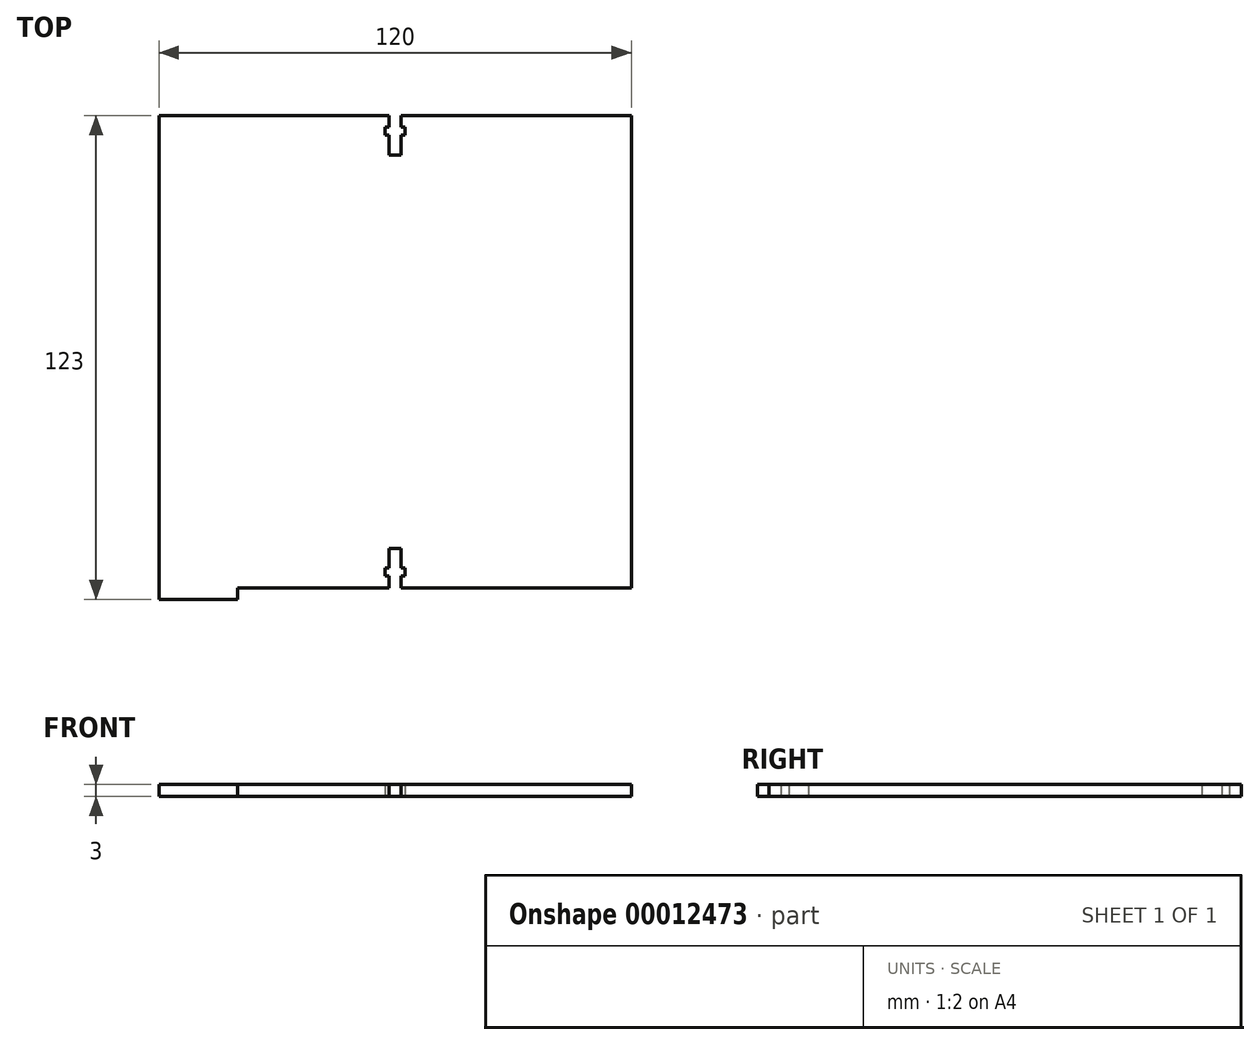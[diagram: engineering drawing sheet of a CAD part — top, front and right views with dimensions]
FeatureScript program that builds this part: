
annotation { "Feature Type Name" : "Feature", "Feature Type Description" : "" }
export const myFeature = defineFeature(function(context is Context, id is Id, definition is map)
    precondition{}
    {
        {
            var Q0;
            Q0=qCreatedBy(makeId("Top.planeOp"),FACE);
            var sketch = newSketch(context, id + "F0", { "sketchPlane" : qUnion([Q0])});
            skLineSegment(sketch, "E0.bottom", {"start": v(-57.37, 59.42) * mm, "end": v(62.63, 59.42) * mm});
            skLineSegment(sketch, "E0.top", {"start": v(-57.37, -60.58) * mm, "end": v(62.63, -60.58) * mm});
            skLineSegment(sketch, "E0.left", {"start": v(-57.37, 59.42) * mm, "end": v(-57.37, -60.58) * mm});
            skLineSegment(sketch, "E0.right", {"start": v(62.63, 59.42) * mm, "end": v(62.63, -60.58) * mm});
            skLineSegment(sketch, "E1.bottom", {"start": v(-57.37, 59.42) * mm, "end": v(-37.37, 59.42) * mm});
            skLineSegment(sketch, "E1.top", {"start": v(-57.37, 62.42) * mm, "end": v(-37.37, 62.42) * mm});
            skLineSegment(sketch, "E1.left", {"start": v(-57.37, 59.42) * mm, "end": v(-57.37, 62.42) * mm});
            skLineSegment(sketch, "E1.right", {"start": v(-37.37, 59.42) * mm, "end": v(-37.37, 62.42) * mm});
            skLineSegment(sketch, "E2.bottom", {"start": v(62.63, 59.42) * mm, "end": v(42.63, 59.42) * mm});
            skLineSegment(sketch, "E2.top", {"start": v(62.63, 62.42) * mm, "end": v(42.63, 62.42) * mm});
            skLineSegment(sketch, "E2.left", {"start": v(62.63, 59.42) * mm, "end": v(62.63, 62.42) * mm});
            skLineSegment(sketch, "E2.right", {"start": v(42.63, 59.42) * mm, "end": v(42.63, 62.42) * mm});
            skLineSegment(sketch, "E3.bottom", {"start": v(-57.37, -60.58) * mm, "end": v(-37.37, -60.58) * mm});
            skLineSegment(sketch, "E3.top", {"start": v(-57.37, -63.58) * mm, "end": v(-37.37, -63.58) * mm});
            skLineSegment(sketch, "E3.left", {"start": v(-57.37, -60.58) * mm, "end": v(-57.37, -63.58) * mm});
            skLineSegment(sketch, "E3.right", {"start": v(-37.37, -60.58) * mm, "end": v(-37.37, -63.58) * mm});
            skLineSegment(sketch, "E4.bottom", {"start": v(62.63, -60.58) * mm, "end": v(42.63, -60.58) * mm});
            skLineSegment(sketch, "E4.top", {"start": v(62.63, -63.58) * mm, "end": v(42.63, -63.58) * mm});
            skLineSegment(sketch, "E4.left", {"start": v(62.63, -60.58) * mm, "end": v(62.63, -63.58) * mm});
            skLineSegment(sketch, "E4.right", {"start": v(42.63, -60.58) * mm, "end": v(42.63, -63.58) * mm});
            skLineSegment(sketch, "E5", {"start": v(-57.37, -0.58) * mm, "end": v(62.63, -0.58) * mm, "construction": true});
            skLineSegment(sketch, "E6", {"start": v(2.63, 59.42) * mm, "end": v(2.63, -60.58) * mm, "construction": true});
            skLineSegment(sketch, "E7", {"start": v(4.13, 59.42) * mm, "end": v(4.13, 56.42) * mm});
            skLineSegment(sketch, "E8", {"start": v(4.13, 56.42) * mm, "end": v(5.13, 56.42) * mm});
            skLineSegment(sketch, "E9", {"start": v(5.13, 56.42) * mm, "end": v(5.13, 54.42) * mm});
            skLineSegment(sketch, "E10", {"start": v(5.13, 54.42) * mm, "end": v(4.13, 54.42) * mm});
            skLineSegment(sketch, "E11", {"start": v(4.13, 54.42) * mm, "end": v(4.13, 49.42) * mm});
            skLineSegment(sketch, "E12", {"start": v(4.13, 49.42) * mm, "end": v(1.13, 49.42) * mm});
            skLineSegment(sketch, "E13", {"start": v(1.13, 49.42) * mm, "end": v(1.13, 54.42) * mm});
            skLineSegment(sketch, "E14", {"start": v(1.13, 54.42) * mm, "end": v(0.13, 54.42) * mm});
            skLineSegment(sketch, "E15", {"start": v(0.13, 54.42) * mm, "end": v(0.13, 56.42) * mm});
            skLineSegment(sketch, "E16", {"start": v(0.13, 56.42) * mm, "end": v(1.13, 56.42) * mm});
            skLineSegment(sketch, "E17", {"start": v(1.13, 56.42) * mm, "end": v(1.13, 59.42) * mm});
            skLineSegment(sketch, "E18.0.MirrorCS", {"start": v(1.13, -55.58) * mm, "end": v(0.13, -55.58) * mm});
            skLineSegment(sketch, "E18.1.MirrorCS", {"start": v(0.13, -55.58) * mm, "end": v(0.13, -57.58) * mm});
            skLineSegment(sketch, "E18.2.MirrorCS", {"start": v(0.13, -57.58) * mm, "end": v(1.13, -57.58) * mm});
            skLineSegment(sketch, "E18.3.MirrorCS", {"start": v(1.13, -57.58) * mm, "end": v(1.13, -60.58) * mm});
            skLineSegment(sketch, "E18.4.MirrorCS", {"start": v(4.13, -60.58) * mm, "end": v(4.13, -57.58) * mm});
            skLineSegment(sketch, "E18.5.MirrorCS", {"start": v(4.13, -57.58) * mm, "end": v(5.13, -57.58) * mm});
            skLineSegment(sketch, "E18.6.MirrorCS", {"start": v(5.13, -57.58) * mm, "end": v(5.13, -55.58) * mm});
            skLineSegment(sketch, "E18.7.MirrorCS", {"start": v(5.13, -55.58) * mm, "end": v(4.13, -55.58) * mm});
            skLineSegment(sketch, "E18.8.MirrorCS", {"start": v(4.13, -55.58) * mm, "end": v(4.13, -50.58) * mm});
            skLineSegment(sketch, "E18.9.MirrorCS", {"start": v(4.13, -50.58) * mm, "end": v(1.13, -50.58) * mm});
            skLineSegment(sketch, "E18.10.MirrorCS", {"start": v(1.13, -50.58) * mm, "end": v(1.13, -55.58) * mm});
            skSolve(sketch);
        }
        {
            var Q0;
            {var subQ9=sQuery(id+"F0.wireOp",EDGE,"E0.left");Q0=makeQuery(id+"F0.imprint","IMPRINT",FACE,{"disambiguationData":[TD([[makeQuery(id+"F0.imprint","IMPRINT",EDGE,{"derivedFrom":subQ9}),1.0]])]});}
            var Q1;
            Q1=makeQuery(id+"F0.imprint","IMPRINT",FACE,{"disambiguationData":[TD([[makeQuery(id+"F0.imprint","IMPRINT",EDGE,{"derivedFrom":sQuery(id+"F0.wireOp",EDGE,"E2.bottom")}),-1.0]])]});
            var Q2;
            Q2=makeQuery(id+"F0.imprint","IMPRINT",FACE,{"disambiguationData":[TD([[makeQuery(id+"F0.imprint","IMPRINT",EDGE,{"derivedFrom":sQuery(id+"F0.wireOp",EDGE,"E1.bottom")}),1.0]])]});
            var Q3;
            {var subQ1=sQuery(id+"F0.wireOp",EDGE,"E3.right");Q3=makeQuery(id+"F0.imprint","IMPRINT",FACE,{"disambiguationData":[TD([[makeQuery(id+"F0.imprint","IMPRINT",EDGE,{"derivedFrom":subQ1}),-1.0]])]});}
            var Q4;
            Q4=makeQuery(id+"F0.imprint","IMPRINT",FACE,{"disambiguationData":[TD([[makeQuery(id+"F0.imprint","IMPRINT",EDGE,{"derivedFrom":sQuery(id+"F0.wireOp",EDGE,"E4.right")}),1.0]])]});
            extrude(context, id + "F1", {"entities" : qUnion([Q0, Q1, Q2, Q3, Q4]), "depth" : 3 * mm});
        }
    });
